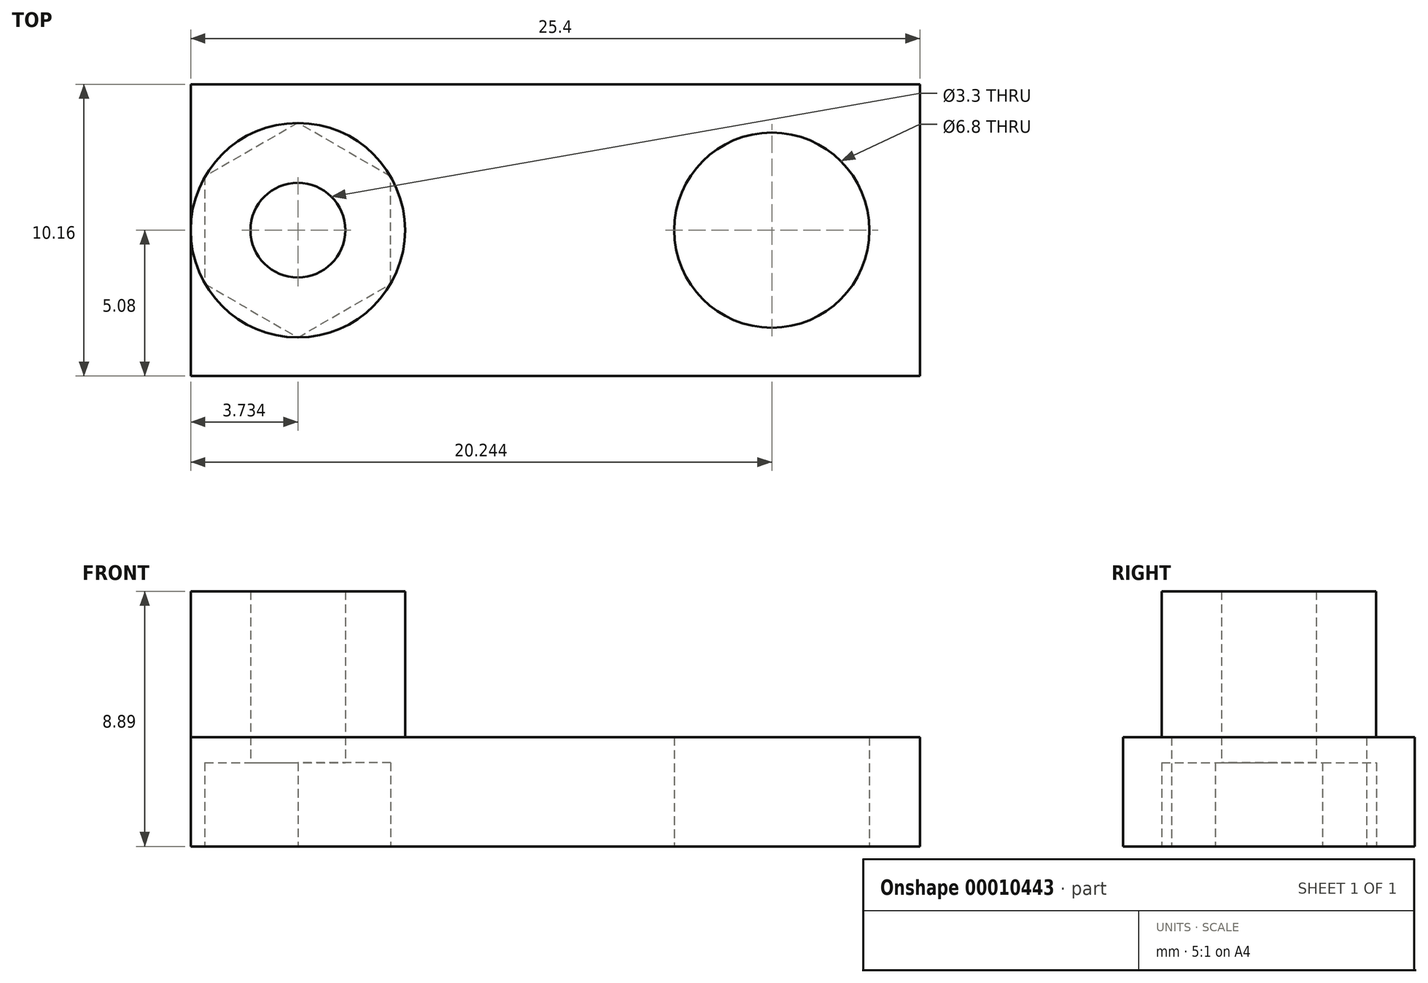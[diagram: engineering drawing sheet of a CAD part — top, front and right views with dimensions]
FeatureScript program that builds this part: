
annotation { "Feature Type Name" : "Feature", "Feature Type Description" : "" }
export const myFeature = defineFeature(function(context is Context, id is Id, definition is map)
    precondition{}
    {
        {
            var Q0;
            Q0=qCreatedBy(makeId("Top.planeOp"),FACE);
            var sketch = newSketch(context, id + "F0", { "sketchPlane" : qUnion([Q0])});
            skLineSegment(sketch, "E0.rect.bottom", {"start": v(-12.7, 5.08) * mm, "end": v(12.7, 5.08) * mm});
            skLineSegment(sketch, "E0.rect.top", {"start": v(-12.7, -5.08) * mm, "end": v(12.7, -5.08) * mm});
            skLineSegment(sketch, "E0.rect.left", {"start": v(-12.7, 5.08) * mm, "end": v(-12.7, -5.08) * mm});
            skLineSegment(sketch, "E0.rect.right", {"start": v(12.7, 5.08) * mm, "end": v(12.7, -5.08) * mm});
            skPoint(sketch, "E0.rect.middle", {"position": v(0, 0) * mm});
            skCircle(sketch, "E1", {"center": v(-8.97, 0) * mm, "radius": 1.65 * mm});
            skCircle(sketch, "E2", {"center": v(7.54, 0) * mm, "radius": 3.4 * mm});
            skSolve(sketch);
        }
        {
            var Q0;
            Q0 = qSketchRegion(id + "F0", true);
            extrude(context, id + "F1", {"entities" : qUnion([Q0]), "depth" : 3.8 * mm});
        }
        {
            var Q0;
            Q0=makeQuery(id+"F1.opExtrude","CAP_FACE",FACE,{"disambiguationData":[OSD([sQuery(id+"F0.wireOp",EDGE,"E0.rect.bottom"),sQuery(id+"F0.wireOp",EDGE,"E0.rect.top"),sQuery(id+"F0.wireOp",EDGE,"E0.rect.left"),sQuery(id+"F0.wireOp",EDGE,"E0.rect.right"),sQuery(id+"F0.wireOp",EDGE,"E1"),sQuery(id+"F0.wireOp",EDGE,"E2")])],"isStart":false});
            var sketch = newSketch(context, id + "F2", { "sketchPlane" : qUnion([Q0])});
            skCircle(sketch, "E3", {"center": v(-8.97, 0) * mm, "radius": 3.73 * mm});
            skCircle(sketch, "E4", {"center": v(-8.97, 0) * mm, "radius": 1.65 * mm});
            skSolve(sketch);
        }
        {
            var Q0;
            Q0 = qSketchRegion(id + "F2", true);
            extrude(context, id + "F3", {"entities" : qUnion([Q0]), "operationType" : NewBodyOperationType.ADD, "depth" : 5.08 * mm});
        }
        {
            var Q0;
            Q0=makeQuery(id+"F1.opExtrude","CAP_FACE",FACE,{"disambiguationData":[OSD([sQuery(id+"F0.wireOp",EDGE,"E0.rect.bottom"),sQuery(id+"F0.wireOp",EDGE,"E0.rect.top"),sQuery(id+"F0.wireOp",EDGE,"E0.rect.left"),sQuery(id+"F0.wireOp",EDGE,"E0.rect.right"),sQuery(id+"F0.wireOp",EDGE,"E1"),sQuery(id+"F0.wireOp",EDGE,"E2")])],"isStart":true});
            var sketch = newSketch(context, id + "F4", { "sketchPlane" : qUnion([Q0])});
            skCircle(sketch, "E5.cCircle", {"center": v(-8.97, 0) * mm, "radius": 3.74 * mm, "construction": true});
            skLineSegment(sketch, "E5.0", {"start": v(-5.73, -1.87) * mm, "end": v(-8.97, -3.74) * mm});
            skLineSegment(sketch, "E5.1", {"start": v(-8.97, -3.74) * mm, "end": v(-12.2, -1.87) * mm});
            skLineSegment(sketch, "E5.2", {"start": v(-12.2, -1.87) * mm, "end": v(-12.2, 1.87) * mm});
            skLineSegment(sketch, "E5.3", {"start": v(-12.2, 1.87) * mm, "end": v(-8.97, 3.74) * mm});
            skLineSegment(sketch, "E5.4", {"start": v(-8.97, 3.74) * mm, "end": v(-5.73, 1.87) * mm});
            skLineSegment(sketch, "E5.5", {"start": v(-5.73, 1.87) * mm, "end": v(-5.73, -1.87) * mm});
            skSolve(sketch);
        }
        {
            var Q0;
            Q0 = qSketchRegion(id + "F4", true);
            extrude(context, id + "F5", {"entities" : qUnion([Q0]), "operationType" : NewBodyOperationType.REMOVE, "oppositeDirection" : true, "depth" : 2.92 * mm});
        }
    });
